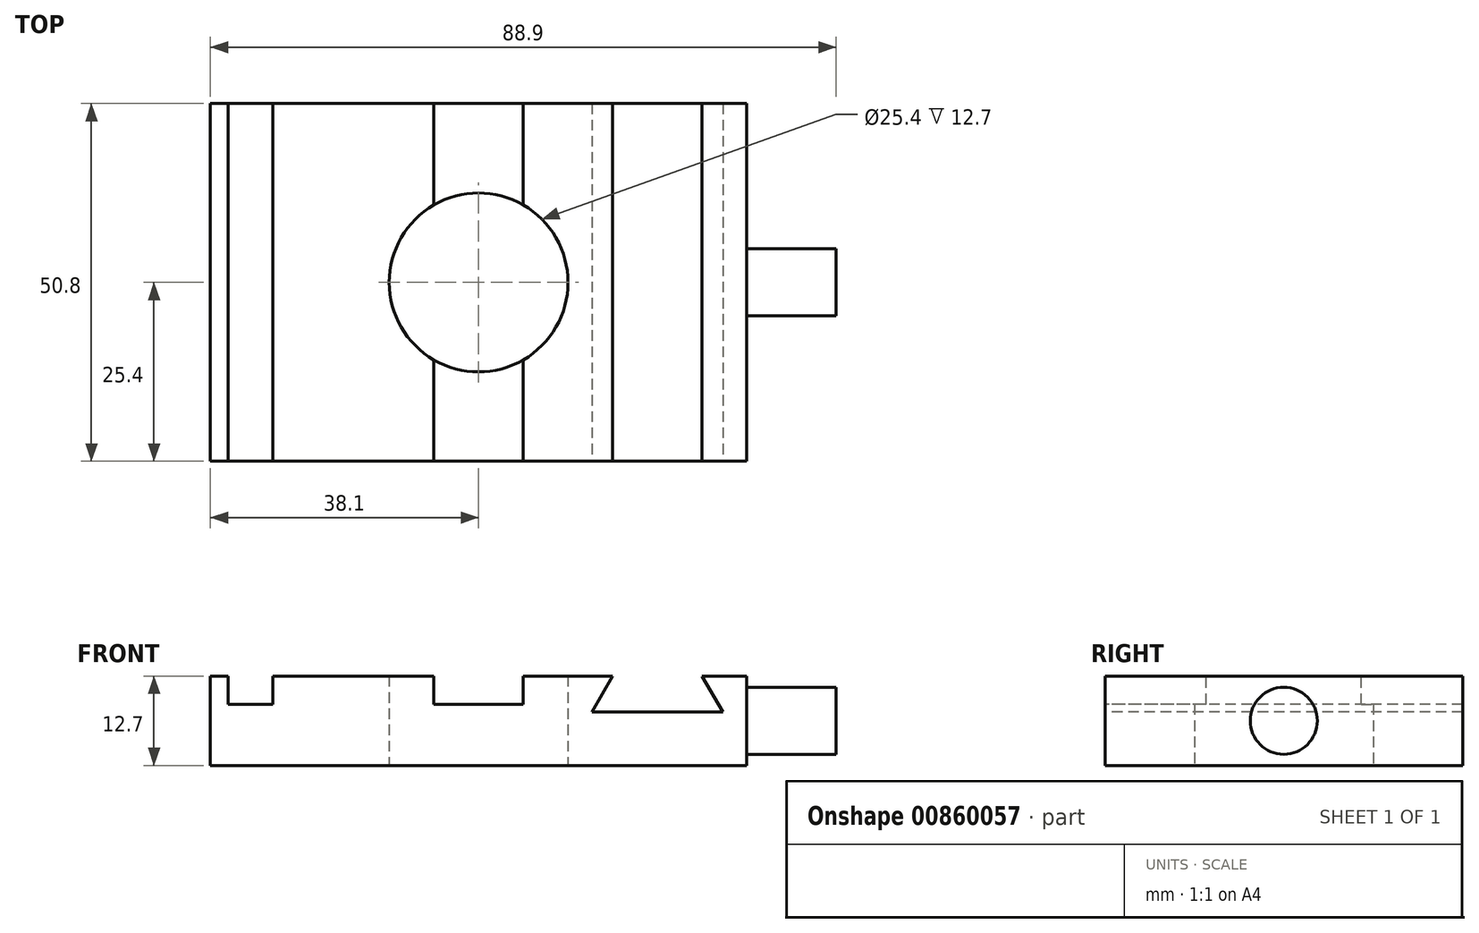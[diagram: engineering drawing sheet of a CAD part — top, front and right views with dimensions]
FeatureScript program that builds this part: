
annotation { "Feature Type Name" : "Feature", "Feature Type Description" : "" }
export const myFeature = defineFeature(function(context is Context, id is Id, definition is map)
    precondition{}
    {
        {
            var Q0;
            Q0=qCreatedBy(makeId("Top.planeOp"),FACE);
            var sketch = newSketch(context, id + "F0", { "sketchPlane" : qUnion([Q0])});
            skLineSegment(sketch, "E0.bottom", {"start": v(-38.1, 25.4) * mm, "end": v(38.1, 25.4) * mm});
            skLineSegment(sketch, "E0.top", {"start": v(-38.1, -25.4) * mm, "end": v(38.1, -25.4) * mm});
            skLineSegment(sketch, "E0.left", {"start": v(-38.1, 25.4) * mm, "end": v(-38.1, -25.4) * mm});
            skLineSegment(sketch, "E0.right", {"start": v(38.1, 25.4) * mm, "end": v(38.1, -25.4) * mm});
            skPoint(sketch, "E0.middle", {"position": v(0, 0) * mm});
            skCircle(sketch, "E1", {"center": v(0, 0) * mm, "radius": 12.7 * mm});
            skSolve(sketch);
        }
        {
            var Q0;
            Q0=makeQuery(id+"F0.imprint","IMPRINT",FACE,{"disambiguationData":[TD([[makeQuery(id+"F0.imprint","IMPRINT",EDGE,{"derivedFrom":sQuery(id+"F0.wireOp",EDGE,"E0.bottom")}),-1.0]])]});
            extrude(context, id + "F1", {"entities" : qUnion([Q0]), "depth" : 12.7 * mm, "offsetDistance" : 25 * mm});
        }
        {
            var Q0;
            Q0=makeQuery(id+"F1.opExtrude","CAP_FACE",FACE,{"disambiguationData":[OSD([sQuery(id+"F0.wireOp",EDGE,"E0.bottom"),sQuery(id+"F0.wireOp",EDGE,"E0.top"),sQuery(id+"F0.wireOp",EDGE,"E0.left"),sQuery(id+"F0.wireOp",EDGE,"E0.right"),sQuery(id+"F0.wireOp",EDGE,"E1")])],"isStart":false});
            var sketch = newSketch(context, id + "F2", { "sketchPlane" : qUnion([Q0])});
            skLineSegment(sketch, "E2.bottom", {"start": v(-35.56, 25.4) * mm, "end": v(-29.21, 25.4) * mm});
            skLineSegment(sketch, "E2.top", {"start": v(-35.56, -25.4) * mm, "end": v(-29.21, -25.4) * mm});
            skLineSegment(sketch, "E2.left", {"start": v(-35.56, 25.4) * mm, "end": v(-35.56, -25.4) * mm});
            skLineSegment(sketch, "E2.right", {"start": v(-29.21, 25.4) * mm, "end": v(-29.21, -25.4) * mm});
            skPoint(sketch, "E3", {"position": v(0, 0) * mm});
            skLineSegment(sketch, "E4", {"start": v(-6.35, 25.4) * mm, "end": v(-6.35, -25.4) * mm});
            skLineSegment(sketch, "E5", {"start": v(-6.35, -25.4) * mm, "end": v(6.35, -25.4) * mm});
            skLineSegment(sketch, "E6", {"start": v(6.35, -25.4) * mm, "end": v(6.35, 25.4) * mm});
            skLineSegment(sketch, "E7", {"start": v(6.35, 25.4) * mm, "end": v(-6.35, 25.4) * mm});
            skLineSegment(sketch, "E8", {"start": v(0, 25.4) * mm, "end": v(0, -25.4) * mm, "construction": true});
            skSolve(sketch);
        }
        {
            var Q0;
            Q0=makeQuery(id+"F2.imprint","IMPRINT",FACE,{"disambiguationData":[TD([[makeQuery(id+"F2.imprint","IMPRINT",EDGE,{"derivedFrom":sQuery(id+"F2.wireOp",EDGE,"E2.bottom")}),-1.0]])]});
            var Q1;
            {var subQ0=sQuery(id+"F2.wireOp",EDGE,"E5");Q1=makeQuery(id+"F2.imprint","IMPRINT",FACE,{"disambiguationData":[TD([[makeQuery(id+"F2.imprint","IMPRINT",EDGE,{"derivedFrom":subQ0}),1.0]])]});}
            var Q2;
            {var subQ0=sQuery(id+"F2.wireOp",EDGE,"E7");Q2=makeQuery(id+"F2.imprint","IMPRINT",FACE,{"disambiguationData":[TD([[makeQuery(id+"F2.imprint","IMPRINT",EDGE,{"derivedFrom":subQ0}),-1.0]])]});}
            extrude(context, id + "F3", {"entities" : qUnion([Q0, Q1, Q2]), "operationType" : NewBodyOperationType.REMOVE, "oppositeDirection" : true, "depth" : 4 * mm, "offsetDistance" : 25 * mm});
        }
        {
            var Q0;
            Q0=makeQuery(id+"F1.opExtrude","SWEPT_FACE",FACE,{"disambiguationData":[OSD([sQuery(id+"F0.wireOp",EDGE,"E0.top")])]});
            var sketch = newSketch(context, id + "F4", { "sketchPlane" : qUnion([Q0])});
            skLineSegment(sketch, "E9", {"start": v(19.05, 12.7) * mm, "end": v(16.12, 7.62) * mm});
            skLineSegment(sketch, "E10", {"start": v(16.12, 7.62) * mm, "end": v(34.68, 7.62) * mm});
            skLineSegment(sketch, "E11", {"start": v(34.68, 7.62) * mm, "end": v(31.75, 12.7) * mm});
            skLineSegment(sketch, "E12", {"start": v(31.75, 12.7) * mm, "end": v(19.05, 12.7) * mm});
            skLineSegment(sketch, "E13", {"start": v(25.4, 7.62) * mm, "end": v(25.4, 12.7) * mm, "construction": true});
            skSolve(sketch);
        }
        {
            var Q0;
            Q0=makeQuery(id+"F4.imprint","IMPRINT",FACE,{"disambiguationData":[TD([[makeQuery(id+"F4.imprint","IMPRINT",EDGE,{"derivedFrom":sQuery(id+"F4.wireOp",EDGE,"E9")}),1.0]])]});
            extrude(context, id + "F5", {"entities" : qUnion([Q0]), "operationType" : NewBodyOperationType.REMOVE, "endBound" : BoundingType.THROUGH_ALL, "oppositeDirection" : true, "depth" : 25 * mm, "offsetDistance" : 25 * mm});
        }
        {
            var Q0;
            Q0=makeQuery(id+"F1.opExtrude","SWEPT_FACE",FACE,{"disambiguationData":[OSD([sQuery(id+"F0.wireOp",EDGE,"E0.right")])]});
            var sketch = newSketch(context, id + "F6", { "sketchPlane" : qUnion([Q0])});
            skPoint(sketch, "E14", {"position": v(0, 6.35) * mm});
            skPoint(sketch, "E14.positionSnap0", {"position": v(-25.4, 6.35) * mm});
            skPoint(sketch, "E14.positionSnap1", {"position": v(0, 12.7) * mm});
            skCircle(sketch, "E15", {"center": v(0, 6.35) * mm, "radius": 4.76 * mm});
            skSolve(sketch);
        }
        {
            var Q0;
            Q0=makeQuery(id+"F6.imprint","IMPRINT",FACE,{"disambiguationData":[TD([[makeQuery(id+"F6.imprint","IMPRINT",EDGE,{"derivedFrom":sQuery(id+"F6.wireOp",EDGE,"E15")}),1.0]])]});
            extrude(context, id + "F7", {"entities" : qUnion([Q0]), "operationType" : NewBodyOperationType.ADD, "depth" : 12.7 * mm, "offsetDistance" : 25 * mm});
        }
    });
